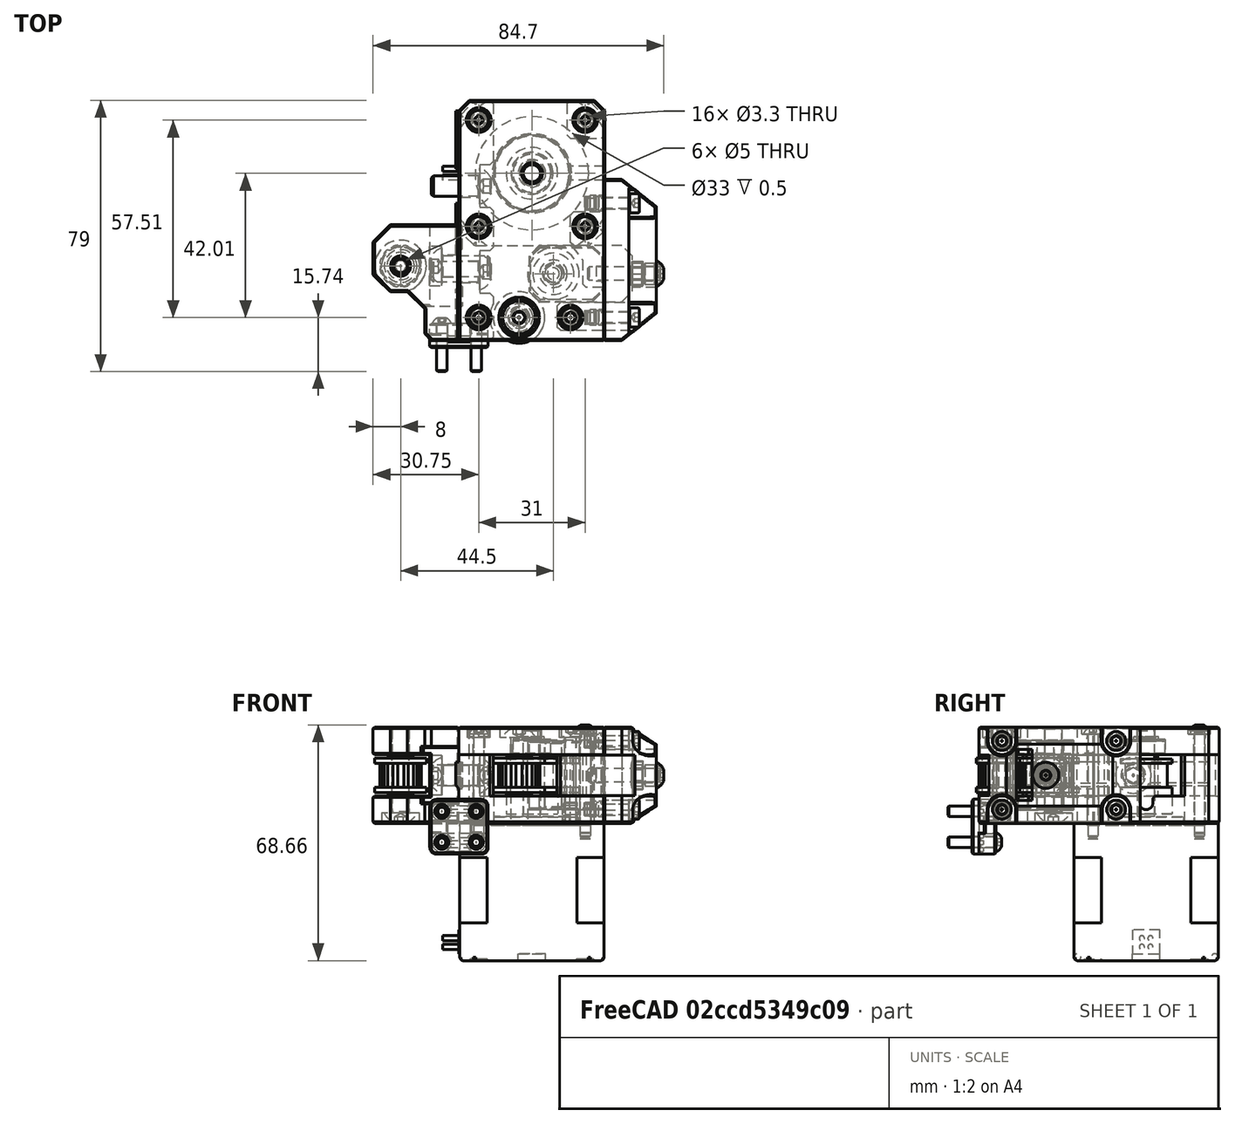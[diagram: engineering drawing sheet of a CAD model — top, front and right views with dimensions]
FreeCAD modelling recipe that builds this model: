
FCSTD DOCUMENT  (FreeCAD 0.19R)
Label: 4PR-assembly
License: All rights reserved
LicenseURL: http://en.wikipedia.org/wiki/All_rights_reserved
objects: Part::FeaturePython×29, Part::Feature×14, App::Part×4
note: 43 computed .brp shape members not serialized (recipe doc carries the construction recipe); baked Part::Feature solids carry a one-line shape summary decoded from their .brp

FEATURE [Part::Feature] Fusion006002011004053036004001001001  label="motor"
  Placement = pos=(21.25,48.75,-39) rot=(0,0,-1;1.5708rad)
  shape: bbox 47 x 42 x 67 mm, 100 faces (baked)
FEATURE [Part::Feature] Cut002001001  label="20t-pulley-6mm"
  Placement = pos=(21.25,48.75,19.7) rot=(0,1,0;3.14159rad)
  shape: bbox 15 x 15 x 16 mm, 8 faces (baked)
FEATURE [Part::Feature] Cut002008018001  label="MR115ZZ"
  Placement = pos=(21.25,48.75,21) rot=(0,0,1;0rad)
  shape: bbox 11 x 11 x 4 mm, 4 faces (baked)
FEATURE [Part::Feature] Cut001001  label="smooth-idler-6mm"
  Placement = pos=(27.5,19.48,10) rot=(0,0,1;0rad)
  shape: bbox 15 x 15 x 10 mm, 8 faces (baked)
FEATURE [Part::Feature] Cut002008019001  label="tooth-idler-6mm"
  Placement = pos=(17.5,6.74,10) rot=(0,0,1;0rad)
  shape: bbox 15 x 15 x 10 mm, 31 faces (baked)
FEATURE [Part::Feature] Body003002003  label="c-motor-mount-inner-plate"
  Placement = pos=(0,0,1) rot=(0,0,1;0rad)
  shape: bbox 43.5 x 70 x 20 mm, 103 faces (baked)
FEATURE [Part::Feature] Body001001  label="c-idler-housing"
  Placement = pos=(27.5,19.5,5) rot=(0,0,1;0rad)
  shape: bbox 21.5 x 16 x 20 mm, 50 faces (baked)
FEATURE [Part::Feature] Body003002001  label="c-tesioner-cap-nut"
  shape: bbox 29.34 x 47 x 28 mm, 105 faces (baked)
FEATURE [Part::Feature] Chamfer002006001  label="c-idler-mount"
  Placement = pos=(0,0,1) rot=(0,0,1;0rad)
  shape: bbox 26 x 33.74 x 28 mm, 108 faces (baked)
FEATURE [Part::Feature] Cut002008019002  label="tooth-idler-6mm001"
  Placement = pos=(-17,21.74,10) rot=(0,0,1;0rad)
  shape: bbox 15 x 15 x 10 mm, 31 faces (baked)
FEATURE [Part::FeaturePython] Screw  label="M5x25-Screw"  # Fasteners workbench fastener (typed FeaturePython)
  Placement = pos=(-17,21.74,4) rot=(1,0,0;3.14159rad)
  baseObject = -> Chamfer002006001 [Edge239]
  diameter = 3
  invert = false
  leftHanded = false
  length = 6
  lengthCustom = 25
  matchOuter = false
  offset = 0
  thread = false
  type = 42
FEATURE [Part::FeaturePython] HeatSet  label="M3-HeatSet"  # Fasteners workbench fastener (typed FeaturePython)
  Placement = pos=(42.5,40,25) rot=(0,1,0;1.5708rad)
  diameter = 3
  invert = false
  leftHanded = false
  matchOuter = false
  offset = 0
  thread = false
  type = 25
FEATURE [Part::FeaturePython] HeatSet001  label="M3-HeatSet001"  # Fasteners workbench fastener (typed FeaturePython)
  Placement = pos=(42.5,6.74,25) rot=(0,1,0;1.5708rad)
  diameter = 3
  invert = false
  leftHanded = false
  matchOuter = false
  offset = 0
  thread = false
  type = 25
FEATURE [Part::FeaturePython] HeatSet002  label="M3-HeatSet002"  # Fasteners workbench fastener (typed FeaturePython)
  Placement = pos=(42.5,40,5.11193) rot=(0,1,0;1.5708rad)
  baseObject = -> Body003002003 [Edge32]
  diameter = 3
  invert = false
  leftHanded = false
  matchOuter = false
  offset = 0
  thread = false
  type = 25
FEATURE [Part::FeaturePython] HeatSet003  label="M3-HeatSet003"  # Fasteners workbench fastener (typed FeaturePython)
  Placement = pos=(42.5,6.74,5.11193) rot=(0,1,0;1.5708rad)
  baseObject = -> Body003002003 [Edge31]
  diameter = 3
  invert = false
  leftHanded = false
  matchOuter = false
  offset = 0
  thread = false
  type = 25
FEATURE [Part::FeaturePython] HeatSet004  label="M3-HeatSet004"  # Fasteners workbench fastener (typed FeaturePython)
  Placement = pos=(32.5,6.74,1) rot=(1,0,0;3.14159rad)
  baseObject = -> Body003002003 [Edge57]
  diameter = 3
  invert = false
  leftHanded = false
  matchOuter = false
  offset = 0
  thread = false
  type = 25
FEATURE [Part::FeaturePython] HeatSet005  label="M3-HeatSet005"  # Fasteners workbench fastener (typed FeaturePython)
  Placement = pos=(5.75,6.74,1) rot=(1,0,0;3.14159rad)
  baseObject = -> Body003002003 [Edge56]
  diameter = 3
  invert = false
  leftHanded = false
  matchOuter = false
  offset = 0
  thread = false
  type = 25
FEATURE [Part::FeaturePython] Screw001  label="M3x25-Screw"  # Fasteners workbench fastener (typed FeaturePython)
  Placement = pos=(5.75,6.74,26) rot=(0,0,1;0rad)
  diameter = 4
  invert = false
  leftHanded = false
  length = 8
  lengthCustom = 25
  matchOuter = false
  offset = 0
  thread = false
  type = 36
FEATURE [Part::FeaturePython] Screw002  label="M3x25-Screw001"  # Fasteners workbench fastener (typed FeaturePython)
  Placement = pos=(32.5,6.74,26) rot=(0,0,1;0rad)
  diameter = 4
  invert = false
  leftHanded = false
  length = 8
  lengthCustom = 25
  matchOuter = false
  offset = 0
  thread = false
  type = 36
FEATURE [Part::FeaturePython] Screw003  label="M3x30-Screw"  # Fasteners workbench fastener (typed FeaturePython)
  Placement = pos=(5.75,64.25,27) rot=(0,0,1;0rad)
  diameter = 1
  invert = false
  leftHanded = false
  length = 8
  lengthCustom = 30
  matchOuter = false
  offset = 0
  thread = false
  type = 42
FEATURE [Part::FeaturePython] Screw004  label="M3x30-Screw007"  # Fasteners workbench fastener (typed FeaturePython)
  Placement = pos=(5.75,33.25,27) rot=(0,0,1;0rad)
  diameter = 1
  invert = false
  leftHanded = false
  length = 8
  lengthCustom = 30
  matchOuter = false
  offset = 0
  thread = false
  type = 42
FEATURE [Part::FeaturePython] Screw005  label="M3x30-Screw008"  # Fasteners workbench fastener (typed FeaturePython)
  Placement = pos=(36.75,33.25,27) rot=(0,0,1;0rad)
  diameter = 1
  invert = false
  leftHanded = false
  length = 8
  lengthCustom = 30
  matchOuter = false
  offset = 0
  thread = false
  type = 42
FEATURE [Part::FeaturePython] Screw006  label="M3x30-Screw009"  # Fasteners workbench fastener (typed FeaturePython)
  Placement = pos=(36.75,64.25,28) rot=(0,0,1;0rad)
  diameter = 1
  invert = false
  leftHanded = false
  length = 8
  lengthCustom = 30
  matchOuter = false
  offset = 0
  thread = false
  type = 42
FEATURE [Part::FeaturePython] Screw007  label="M6x14-Screw"  # Fasteners workbench fastener (typed FeaturePython)
  Placement = pos=(-5,21.74,15) rot=(0,-1,0;1.5708rad)
  baseObject = -> Chamfer002006001 [Edge210]
  diameter = 4
  invert = false
  leftHanded = false
  length = 2
  lengthCustom = 14
  matchOuter = false
  offset = 0
  thread = false
  type = 42
FEATURE [App::Part] Part002  label="C-idler"
  Group = -> [Chamfer002006001,Cut002008019002,Screw,Screw007]
  Origin = -> Origin002
  Placement = pos=(200,0,0) rot=(0,0,1;0rad)
FEATURE [Part::FeaturePython] Screw008  label="M6x14-Screw001"  # Fasteners workbench fastener (typed FeaturePython)
  Placement = pos=(6,45,15) rot=(0,1,0;1.5708rad)
  baseObject = -> Body003002003 [Edge86]
  diameter = 4
  invert = false
  leftHanded = false
  length = 2
  lengthCustom = 14
  matchOuter = false
  offset = 0
  thread = false
  type = 42
FEATURE [Part::FeaturePython] Screw009  label="M6x14-Screw002"  # Fasteners workbench fastener (typed FeaturePython)
  Placement = pos=(6,20,15) rot=(0,1,0;1.5708rad)
  baseObject = -> Body003002003 [Edge93]
  diameter = 4
  invert = false
  leftHanded = false
  length = 2
  lengthCustom = 14
  matchOuter = false
  offset = 0
  thread = false
  type = 42
FEATURE [Part::FeaturePython] Screw010  label="M5x25-Screw001"  # Fasteners workbench fastener (typed FeaturePython)
  Placement = pos=(17.5,6.74,26) rot=(0,0,1;0rad)
  diameter = 3
  invert = false
  leftHanded = false
  length = 6
  lengthCustom = 25
  matchOuter = false
  offset = 0
  thread = false
  type = 42
FEATURE [Part::FeaturePython] Screw011  label="M3x10-Screw"  # Fasteners workbench fastener (typed FeaturePython)
  Placement = pos=(49.5,40,25) rot=(0,1,0;1.5708rad)
  diameter = 4
  invert = false
  leftHanded = false
  length = 3
  lengthCustom = 10
  matchOuter = false
  offset = 0
  thread = false
  type = 36
FEATURE [Part::FeaturePython] Screw012  label="M3x10-Screw004"  # Fasteners workbench fastener (typed FeaturePython)
  Placement = pos=(49.5,6.74,25) rot=(0,1,0;1.5708rad)
  diameter = 4
  invert = false
  leftHanded = false
  length = 3
  lengthCustom = 10
  matchOuter = false
  offset = 0
  thread = false
  type = 36
FEATURE [Part::FeaturePython] Screw013  label="M3x10-Screw005"  # Fasteners workbench fastener (typed FeaturePython)
  Placement = pos=(49.5,6.74,5) rot=(0,1,0;1.5708rad)
  diameter = 4
  invert = false
  leftHanded = false
  length = 3
  lengthCustom = 10
  matchOuter = false
  offset = 0
  thread = false
  type = 36
FEATURE [Part::FeaturePython] Screw014  label="M3x10-Screw006"  # Fasteners workbench fastener (typed FeaturePython)
  Placement = pos=(49.5,40,5) rot=(0,1,0;1.5708rad)
  diameter = 4
  invert = false
  leftHanded = false
  length = 3
  lengthCustom = 10
  matchOuter = false
  offset = 0
  thread = false
  type = 36
FEATURE [Part::FeaturePython] Screw015  label="M4x20-Screw"  # Fasteners workbench fastener (typed FeaturePython)
  Placement = pos=(57.5,19.5,15) rot=(0,1,0;1.5708rad)
  diameter = 2
  invert = false
  leftHanded = false
  length = 6
  lengthCustom = 20
  matchOuter = false
  offset = 0
  thread = false
  type = 42
FEATURE [Part::FeaturePython] HeatSet006  label="M4-HeatSet"  # Fasteners workbench fastener (typed FeaturePython)
  Placement = pos=(50.5,19.5,15) rot=(0,-1,0;1.5708rad)
  diameter = 5
  invert = false
  leftHanded = false
  matchOuter = false
  offset = 0
  thread = false
  type = 25
FEATURE [Part::FeaturePython] ThreadedRod  label="M5x20-ThreadedRod"  # Fasteners workbench fastener (typed FeaturePython)
  Placement = pos=(27.5,19.5,5) rot=(1,0,0;3.14159rad)
  baseObject = -> Body001001 [Edge93]
  diameter = 7
  diameterCustom = 6
  invert = true
  leftHanded = false
  length = 20
  matchOuter = false
  offset = 0
  pitchCustom = 1
  thread = false
  type = 4
FEATURE [Part::FeaturePython] Nut  label="M4-Nut"  # Fasteners workbench fastener (typed FeaturePython)
  Placement = pos=(53.5,19.5,15) rot=(0,-1,0;1.5708rad)
  baseObject = -> Body003002001 [Edge199]
  diameter = 6
  invert = true
  leftHanded = false
  matchOuter = false
  offset = 0
  thread = false
  type = 9
FEATURE [Part::Feature] Pad013001  label="c-motor-mount-outer-plate"
  Placement = pos=(0,0,21) rot=(0,0,1;0rad)
  shape: bbox 42.5 x 70 x 8.85 mm, 70 faces (baked)
FEATURE [Part::Feature] Body003002004  label="c-belt-mounter-top"
  Placement = pos=(0,0,0) rot=(-1,0,0;1.5708rad)
  shape: bbox 17 x 5 x 16 mm, 65 faces (baked)
FEATURE [Part::Feature] Body003002005  label="c-belt-mounter-bottom"
  Placement = pos=(0,-2,0) rot=(-1,0,0;1.5708rad)
  shape: bbox 17 x 4 x 16 mm, 64 faces (baked)
FEATURE [Part::FeaturePython] Screw016  label="M3x14-Screw002"  # Fasteners workbench fastener (typed FeaturePython)
  Placement = pos=(-5,5,4.5) rot=(-1,0,0;1.5708rad)
  baseObject = -> Body003002004 [Edge75]
  diameter = 1
  invert = false
  leftHanded = false
  length = 4
  lengthCustom = 14
  matchOuter = false
  offset = 0
  thread = false
  type = 42
FEATURE [Part::FeaturePython] Screw017  label="M3x14-Screw001"  # Fasteners workbench fastener (typed FeaturePython)
  Placement = pos=(5,5,4.5) rot=(-1,0,0;1.5708rad)
  baseObject = -> Body003002004 [Edge76]
  diameter = 1
  invert = false
  leftHanded = false
  length = 4
  lengthCustom = 14
  matchOuter = false
  offset = 0
  thread = false
  type = 42
FEATURE [Part::FeaturePython] Screw018  label="M3x14-Screw003"  # Fasteners workbench fastener (typed FeaturePython)
  Placement = pos=(-5,5,-4.5) rot=(-1,0,0;1.5708rad)
  baseObject = -> Body003002004 [Edge74]
  diameter = 1
  invert = false
  leftHanded = false
  length = 4
  lengthCustom = 14
  matchOuter = false
  offset = 0
  thread = false
  type = 42
FEATURE [Part::FeaturePython] Screw019  label="M3x14-Screw"  # Fasteners workbench fastener (typed FeaturePython)
  Placement = pos=(5,5,-4.5) rot=(-1,0,0;1.5708rad)
  baseObject = -> Body003002004 [Edge73]
  diameter = 1
  invert = false
  leftHanded = false
  length = 4
  lengthCustom = 14
  matchOuter = false
  offset = 0
  thread = false
  type = 42
FEATURE [App::Part] Part001  label="C-belt-mounter"
  Group = -> [Body003002004,Body003002005,Screw019,Screw017,Screw016,Screw018]
  Origin = -> Origin001
  Placement = pos=(110,0,15) rot=(0,1,0;1.5708rad)
FEATURE [Part::Feature] Tube001  label="c-motor-shaft-spacer"
  Placement = pos=(21.25,48.75,25.25) rot=(0,0,1;0rad)
  shape: bbox 7.3 x 7.3 x 1 mm, 4 faces (baked)
FEATURE [App::Part] Part  label="C-motor-mount"
  Group = -> [Fusion006002011004053036004001001001,Cut002001001,Cut002008018001,Cut001001,Cut002008019001,Body003002003,Body001001,Body003002001,HeatSet,HeatSet001,HeatSet002,HeatSet003,HeatSet004,HeatSet005,Screw001,Screw002,Screw003,Screw004,Screw005,Screw006,Screw008,Screw009,Screw010,Screw011,Screw012,Screw013,Screw014,Screw015,HeatSet006,ThreadedRod,Nut,Pad013001,Tube001]
  Origin = -> Origin
FEATURE [App::Part] Part003  label="4PR-assembly"
  Group = -> [Part,Part001,Part002]
  Origin = -> Origin003
